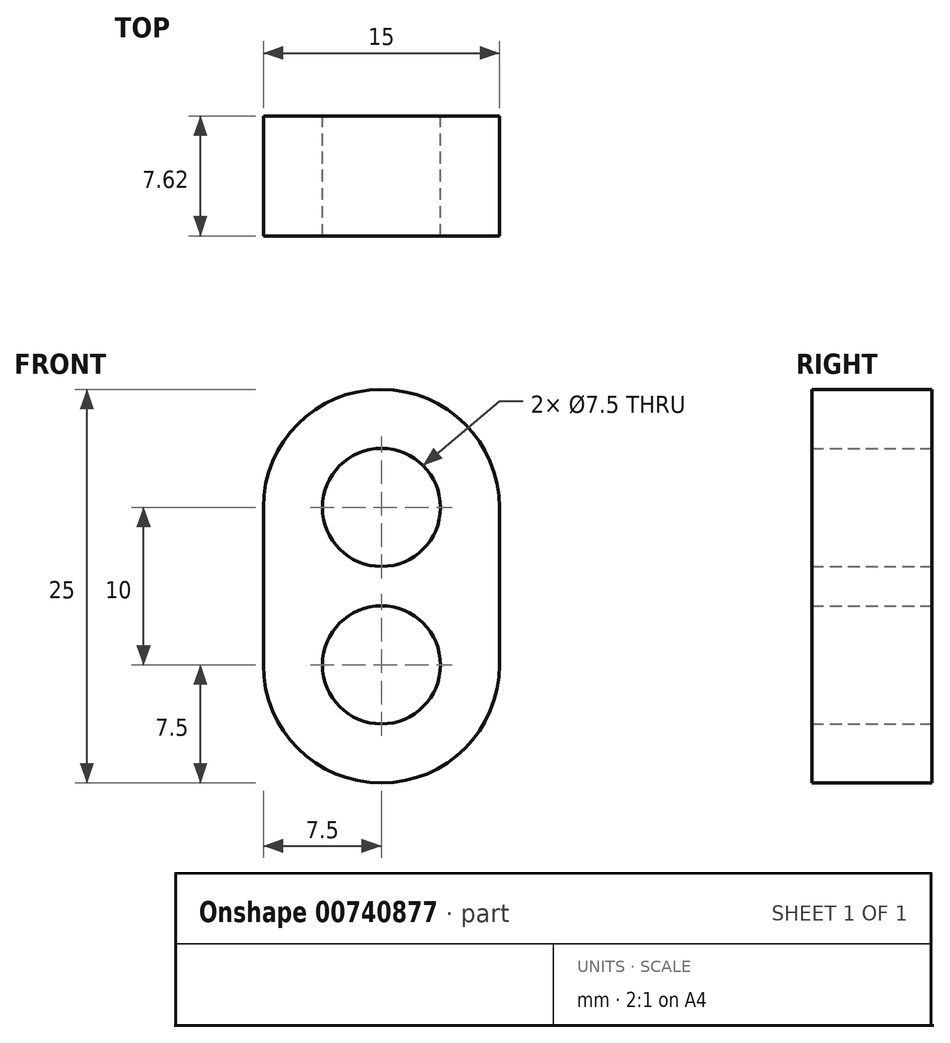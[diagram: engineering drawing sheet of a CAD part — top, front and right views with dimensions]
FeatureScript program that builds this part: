
annotation { "Feature Type Name" : "Feature", "Feature Type Description" : "" }
export const myFeature = defineFeature(function(context is Context, id is Id, definition is map)
    precondition{}
    {
        {
            var Q0;
            Q0=qCreatedBy(makeId("Front.planeOp"),FACE);
            var sketch = newSketch(context, id + "F0", { "sketchPlane" : qUnion([Q0])});
            skCircle(sketch, "E0", {"center": v(0, 0) * mm, "radius": 3.75 * mm});
            skCircle(sketch, "E1", {"center": v(0, 10) * mm, "radius": 3.75 * mm});
            skCircle(sketch, "E2", {"center": v(0, 10) * mm, "radius": 7.5 * mm});
            skCircle(sketch, "E3", {"center": v(0, 0) * mm, "radius": 7.5 * mm});
            skLineSegment(sketch, "E4", {"start": v(-7.5, 0) * mm, "end": v(-7.5, 10) * mm});
            skLineSegment(sketch, "E5", {"start": v(7.5, 10) * mm, "end": v(7.5, 0) * mm});
            skSolve(sketch);
        }
        {
            var Q0;
            {var subQ2=sQuery(id+"F0.wireOp",EDGE,"E3");var subQ6=sQuery(id+"F0.wireOp",EDGE,"E1");var subQ7=makeQuery(id+"F0.imprint","INTERSECT",VERTEX,{"disambiguationData":[OD(0.0)],"derivedFrom":[subQ6,subQ2]});Q0=makeQuery(id+"F0.imprint","IMPRINT",FACE,{"disambiguationData":[TD([[makeQuery(id+"F0.imprint","IMPRINT",EDGE,{"disambiguationData":[TD([[subQ7,-1.0]])],"derivedFrom":subQ6}),-1.0]])]});}
            var Q1;
            {var subQ0=sQuery(id+"F0.wireOp",EDGE,"E2");var subQ1=sQuery(id+"F0.wireOp",EDGE,"E0");var subQ5=makeQuery(id+"F0.imprint","INTERSECT",VERTEX,{"disambiguationData":[OD(0.0)],"derivedFrom":[subQ1,subQ0]});Q1=makeQuery(id+"F0.imprint","IMPRINT",FACE,{"disambiguationData":[TD([[makeQuery(id+"F0.imprint","IMPRINT",EDGE,{"disambiguationData":[TD([[subQ5,1.0]])],"derivedFrom":subQ1}),-1.0]])]});}
            var Q2;
            {var subQ2=sQuery(id+"F0.wireOp",EDGE,"E2");var subQ4=sQuery(id+"F0.wireOp",EDGE,"E0");var subQ6=makeQuery(id+"F0.imprint","INTERSECT",VERTEX,{"disambiguationData":[OD(0.0)],"derivedFrom":[subQ4,subQ2]});Q2=makeQuery(id+"F0.imprint","IMPRINT",FACE,{"disambiguationData":[TD([[makeQuery(id+"F0.imprint","IMPRINT",EDGE,{"disambiguationData":[TD([[subQ6,-1.0]])],"derivedFrom":subQ4}),-1.0]])]});}
            var Q3;
            {var subQ0=sQuery(id+"F0.wireOp",EDGE,"E5");Q3=makeQuery(id+"F0.imprint","IMPRINT",FACE,{"disambiguationData":[TD([[makeQuery(id+"F0.imprint","IMPRINT",EDGE,{"derivedFrom":subQ0}),-1.0]])]});}
            var Q4;
            {var subQ0=sQuery(id+"F0.wireOp",EDGE,"E4");Q4=makeQuery(id+"F0.imprint","IMPRINT",FACE,{"disambiguationData":[TD([[makeQuery(id+"F0.imprint","IMPRINT",EDGE,{"derivedFrom":subQ0}),-1.0]])]});}
            extrude(context, id + "F1", {"entities" : qUnion([Q0, Q1, Q2, Q3, Q4]), "depth" : 7.62 * mm, "offsetDistance" : 25.4 * mm});
        }
    });
